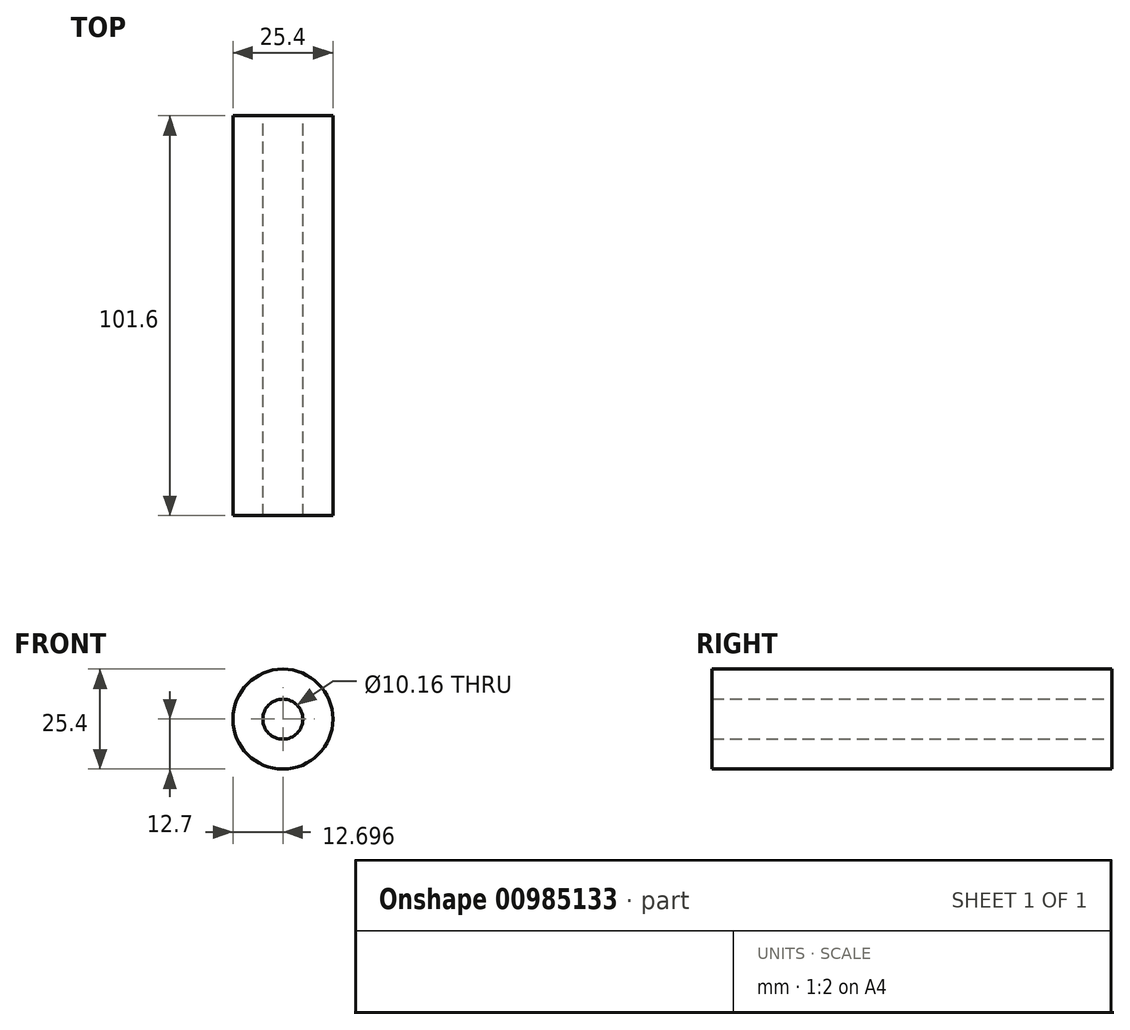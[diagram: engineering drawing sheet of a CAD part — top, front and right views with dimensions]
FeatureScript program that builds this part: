
annotation { "Feature Type Name" : "Feature", "Feature Type Description" : "" }
export const myFeature = defineFeature(function(context is Context, id is Id, definition is map)
    precondition{}
    {
        {
            var Q0;
            Q0=qCreatedBy(makeId("Front.planeOp"),FACE);
            var sketch = newSketch(context, id + "F0", { "sketchPlane" : qUnion([Q0])});
            skCircle(sketch, "E0", {"center": v(-18.46, 8.48) * mm, "radius": 5.08 * mm});
            skCircle(sketch, "E1", {"center": v(-18.46, 8.48) * mm, "radius": 12.7 * mm});
            skSolve(sketch);
        }
        {
            var Q0;
            Q0=makeQuery(id+"F0.imprint","IMPRINT",FACE,{"disambiguationData":[TD([[makeQuery(id+"F0.imprint","IMPRINT",EDGE,{"derivedFrom":sQuery(id+"F0.wireOp",EDGE,"E0")}),-1.0]])]});
            extrude(context, id + "F1", {"entities" : qUnion([Q0]), "depth" : 101.6 * mm, "offsetDistance" : 25.4 * mm});
        }
    });
